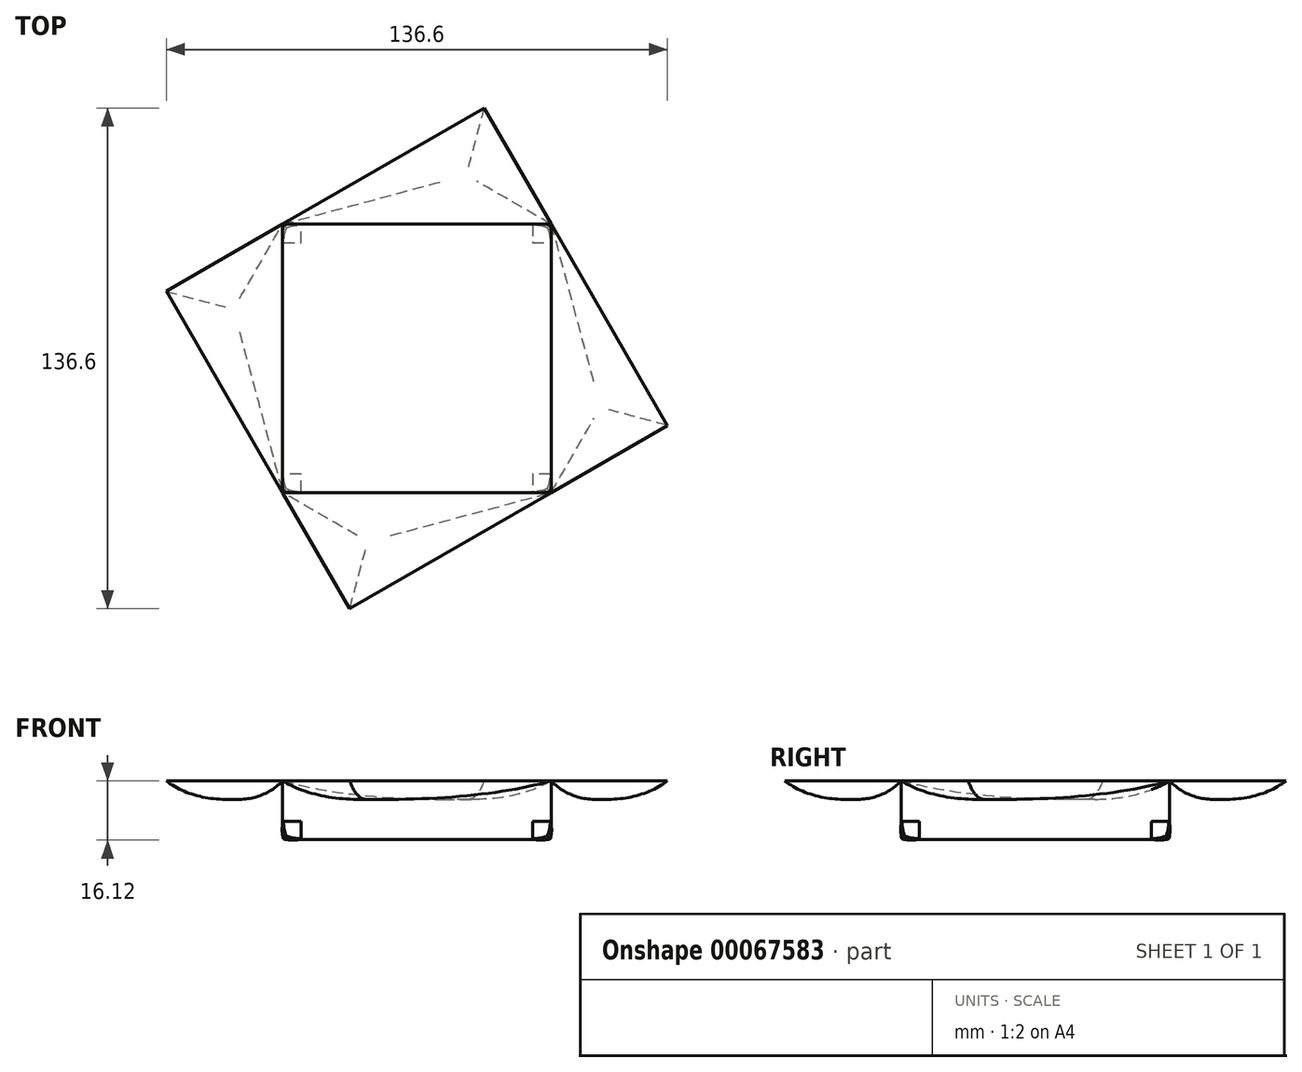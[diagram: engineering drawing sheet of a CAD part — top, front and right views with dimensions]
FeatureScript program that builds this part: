
annotation { "Feature Type Name" : "Feature", "Feature Type Description" : "" }
export const myFeature = defineFeature(function(context is Context, id is Id, definition is map)
    precondition{}
    {
        {
            var Q0;
            Q0=qCreatedBy(makeId("Top.planeOp"),FACE);
            var sketch = newSketch(context, id + "F0", { "sketchPlane" : qUnion([Q0])});
            skLineSegment(sketch, "E0.rect.bottom", {"start": v(36.6, -36.6) * mm, "end": v(-36.6, -36.6) * mm});
            skLineSegment(sketch, "E0.rect.top", {"start": v(36.6, 36.6) * mm, "end": v(-36.6, 36.6) * mm});
            skLineSegment(sketch, "E0.rect.left", {"start": v(36.6, -36.6) * mm, "end": v(36.6, 36.6) * mm});
            skLineSegment(sketch, "E0.rect.right", {"start": v(-36.6, -36.6) * mm, "end": v(-36.6, 36.6) * mm});
            skPoint(sketch, "E0.rect.middle", {"position": v(0, 0) * mm});
            skLineSegment(sketch, "E1", {"start": v(36.6, 36.6) * mm, "end": v(68.3, -18.3) * mm});
            skLineSegment(sketch, "E2", {"start": v(68.3, -18.3) * mm, "end": v(36.6, -36.6) * mm});
            skLineSegment(sketch, "E3.1.0", {"start": v(18.3, 68.3) * mm, "end": v(36.6, 36.6) * mm});
            skLineSegment(sketch, "E3.1.1", {"start": v(-36.6, 36.6) * mm, "end": v(18.3, 68.3) * mm});
            skLineSegment(sketch, "E3.2.0", {"start": v(-68.3, 18.3) * mm, "end": v(-36.6, 36.6) * mm});
            skLineSegment(sketch, "E3.2.1", {"start": v(-36.6, -36.6) * mm, "end": v(-68.3, 18.3) * mm});
            skLineSegment(sketch, "E3.3.0", {"start": v(-18.3, -68.3) * mm, "end": v(-36.6, -36.6) * mm});
            skLineSegment(sketch, "E3.3.1", {"start": v(36.6, -36.6) * mm, "end": v(-18.3, -68.3) * mm});
            skSolve(sketch);
        }
        {
            var Q0;
            Q0=makeQuery(id+"F0.imprint","IMPRINT",FACE,{"disambiguationData":[TD([[makeQuery(id+"F0.imprint","IMPRINT",EDGE,{"derivedFrom":sQuery(id+"F0.wireOp",EDGE,"E0.rect.bottom")}),-1.0]])]});
            extrude(context, id + "F1", {"entities" : qUnion([Q0]), "oppositeDirection" : true, "depth" : 16 * mm});
        }
        {
            var Q0;
            Q0=makeQuery(id+"F0.imprint","IMPRINT",FACE,{"disambiguationData":[TD([[makeQuery(id+"F0.imprint","IMPRINT",EDGE,{"derivedFrom":sQuery(id+"F0.wireOp",EDGE,"E0.rect.right")}),1.0]])]});
            var Q1;
            Q1=makeQuery(id+"F0.imprint","IMPRINT",FACE,{"disambiguationData":[TD([[makeQuery(id+"F0.imprint","IMPRINT",EDGE,{"derivedFrom":sQuery(id+"F0.wireOp",EDGE,"E0.rect.top")}),-1.0]])]});
            var Q2;
            Q2=makeQuery(id+"F0.imprint","IMPRINT",FACE,{"disambiguationData":[TD([[makeQuery(id+"F0.imprint","IMPRINT",EDGE,{"derivedFrom":sQuery(id+"F0.wireOp",EDGE,"E0.rect.left")}),-1.0]])]});
            var Q3;
            Q3=makeQuery(id+"F0.imprint","IMPRINT",FACE,{"disambiguationData":[TD([[makeQuery(id+"F0.imprint","IMPRINT",EDGE,{"derivedFrom":sQuery(id+"F0.wireOp",EDGE,"E0.rect.bottom")}),1.0]])]});
            extrude(context, id + "F2", {"entities" : qUnion([Q0, Q1, Q2, Q3]), "oppositeDirection" : true, "depth" : 5 * mm});
        }
        {
            var Q0;
            Q0=makeQuery(id+"F2.opExtrude","CAP_FACE",FACE,{"disambiguationData":[OSD([sQuery(id+"F0.wireOp",EDGE,"E0.rect.right"),sQuery(id+"F0.wireOp",EDGE,"E3.2.0"),sQuery(id+"F0.wireOp",EDGE,"E3.2.1")])],"isStart":false});
            var Q1;
            Q1=makeQuery(id+"F2.opExtrude","CAP_FACE",FACE,{"disambiguationData":[OSD([sQuery(id+"F0.wireOp",EDGE,"E0.rect.top"),sQuery(id+"F0.wireOp",EDGE,"E3.1.0"),sQuery(id+"F0.wireOp",EDGE,"E3.1.1")])],"isStart":false});
            var Q2;
            Q2=makeQuery(id+"F2.opExtrude","CAP_FACE",FACE,{"disambiguationData":[OSD([sQuery(id+"F0.wireOp",EDGE,"E0.rect.left"),sQuery(id+"F0.wireOp",EDGE,"E1"),sQuery(id+"F0.wireOp",EDGE,"E2")])],"isStart":false});
            var Q3;
            Q3=makeQuery(id+"F2.opExtrude","CAP_FACE",FACE,{"disambiguationData":[OSD([sQuery(id+"F0.wireOp",EDGE,"E0.rect.bottom"),sQuery(id+"F0.wireOp",EDGE,"E3.3.0"),sQuery(id+"F0.wireOp",EDGE,"E3.3.1")])],"isStart":false});
            fillet(context, id + "F3", {"entities" : qUnion([Q0, Q1, Q2, Q3]), "radius" : 16.26 * mm, "tangentPropagation" : true, "allowEdgeOverflow" : false});
        }
        {
            var Q0;
            Q0=makeQuery(id+"F1.opExtrude","CAP_EDGE",EDGE,{"disambiguationData":[OSD([sQuery(id+"F0.wireOp",EDGE,"E0.rect.bottom")])],"isStart":false});
            var Q1;
            Q1=makeQuery(id+"F1.opExtrude","CAP_EDGE",EDGE,{"disambiguationData":[OSD([sQuery(id+"F0.wireOp",EDGE,"E0.rect.right")])],"isStart":false});
            var Q2;
            Q2=makeQuery(id+"F1.opExtrude","CAP_EDGE",EDGE,{"disambiguationData":[OSD([sQuery(id+"F0.wireOp",EDGE,"E0.rect.top")])],"isStart":false});
            var Q3;
            Q3=makeQuery(id+"F1.opExtrude","CAP_EDGE",EDGE,{"disambiguationData":[OSD([sQuery(id+"F0.wireOp",EDGE,"E0.rect.left")])],"isStart":false});
            var Q4;
            Q4=makeQuery(id+"F1.opExtrude","SWEPT_EDGE",EDGE,{"disambiguationData":[OSD([sQuery(id+"F0.wireOp",EDGE,"E0.rect.bottom"),sQuery(id+"F0.wireOp",EDGE,"E0.rect.left"),sQuery(id+"F0.wireOp",EDGE,"E2"),sQuery(id+"F0.wireOp",EDGE,"E3.3.1")])]});
            var Q5;
            Q5=makeQuery(id+"F1.opExtrude","SWEPT_EDGE",EDGE,{"disambiguationData":[OSD([sQuery(id+"F0.wireOp",EDGE,"E0.rect.bottom"),sQuery(id+"F0.wireOp",EDGE,"E0.rect.right"),sQuery(id+"F0.wireOp",EDGE,"E3.2.1"),sQuery(id+"F0.wireOp",EDGE,"E3.3.0")])]});
            var Q6;
            Q6=makeQuery(id+"F1.opExtrude","SWEPT_EDGE",EDGE,{"disambiguationData":[OSD([sQuery(id+"F0.wireOp",EDGE,"E0.rect.top"),sQuery(id+"F0.wireOp",EDGE,"E0.rect.right"),sQuery(id+"F0.wireOp",EDGE,"E3.1.1"),sQuery(id+"F0.wireOp",EDGE,"E3.2.0")])]});
            var Q7;
            Q7=makeQuery(id+"F1.opExtrude","SWEPT_EDGE",EDGE,{"disambiguationData":[OSD([sQuery(id+"F0.wireOp",EDGE,"E0.rect.top"),sQuery(id+"F0.wireOp",EDGE,"E0.rect.left"),sQuery(id+"F0.wireOp",EDGE,"E1"),sQuery(id+"F0.wireOp",EDGE,"E3.1.0")])]});
            fillet(context, id + "F4", {"entities" : qUnion([Q0, Q1, Q2, Q3, Q4, Q5, Q6, Q7]), "radius" : 5 * mm, "tangentPropagation" : true, "rho" : 0.9, "crossSection" : FilletCrossSection.CONIC, "allowEdgeOverflow" : false});
        }
    });
